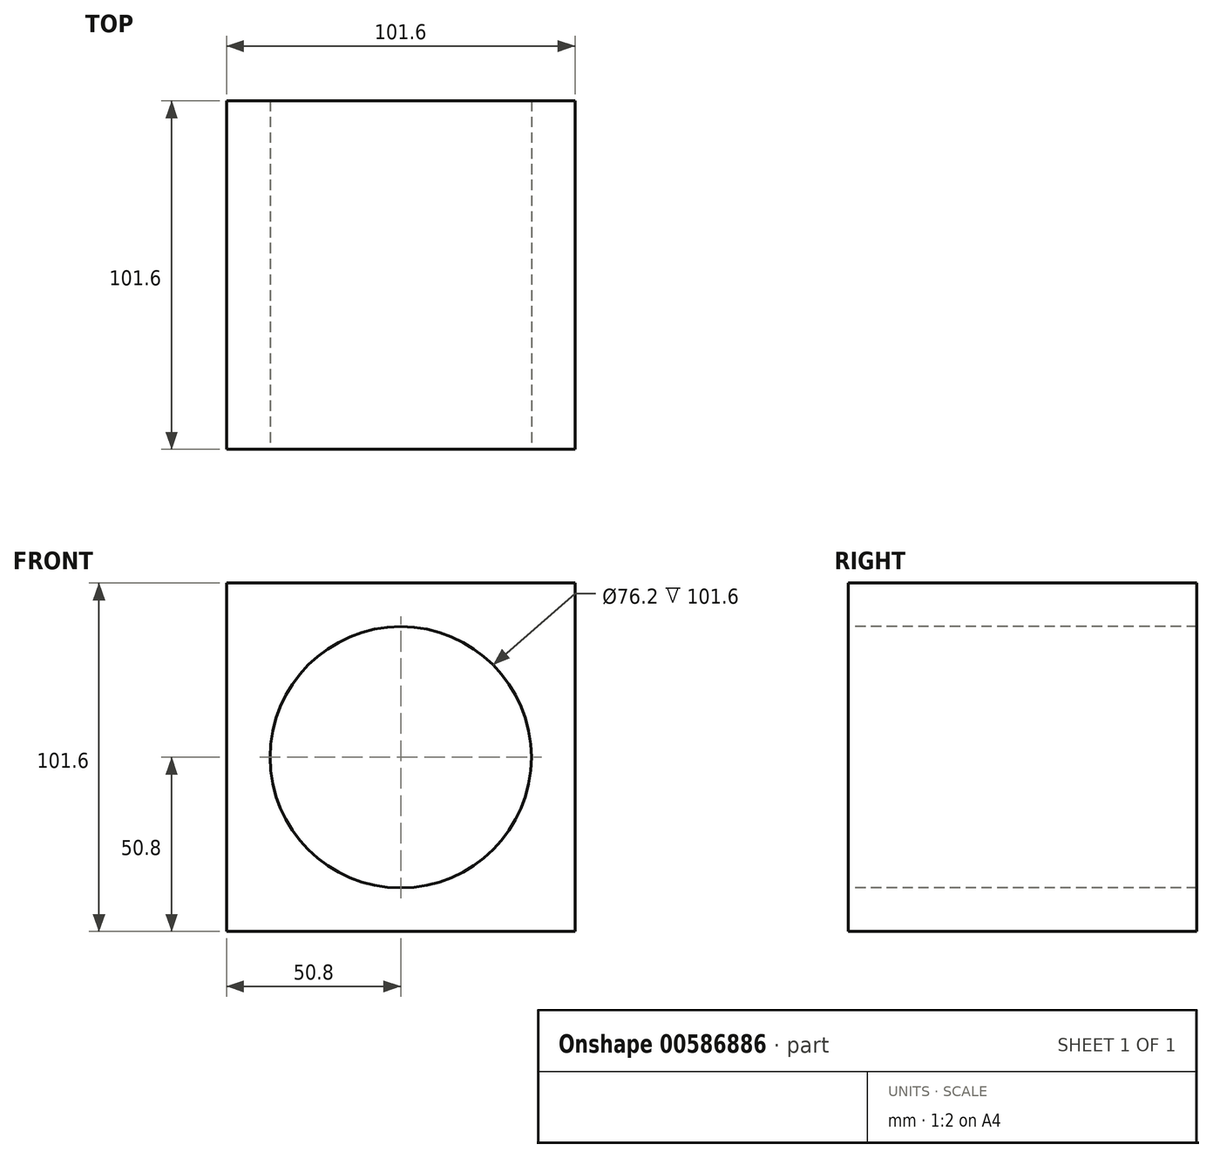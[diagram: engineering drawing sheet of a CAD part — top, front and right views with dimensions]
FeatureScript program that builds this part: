
annotation { "Feature Type Name" : "Feature", "Feature Type Description" : "" }
export const myFeature = defineFeature(function(context is Context, id is Id, definition is map)
    precondition{}
    {
        {
            var Q0;
            Q0=qCreatedBy(makeId("Front.planeOp"),FACE);
            var sketch = newSketch(context, id + "F0", { "sketchPlane" : qUnion([Q0])});
            skLineSegment(sketch, "E0.bottom", {"start": v(0, 0) * mm, "end": v(101.6, 0) * mm});
            skLineSegment(sketch, "E0.top", {"start": v(0, 101.6) * mm, "end": v(101.6, 101.6) * mm});
            skLineSegment(sketch, "E0.left", {"start": v(0, 0) * mm, "end": v(0, 101.6) * mm});
            skLineSegment(sketch, "E0.right", {"start": v(101.6, 0) * mm, "end": v(101.6, 101.6) * mm});
            skSolve(sketch);
        }
        {
            var Q0;
            Q0=makeQuery(id+"F0.imprint","IMPRINT",FACE,{"disambiguationData":[TD([[makeQuery(id+"F0.imprint","IMPRINT",EDGE,{"derivedFrom":sQuery(id+"F0.wireOp",EDGE,"E0.bottom")}),1.0]])]});
            extrude(context, id + "F1", {"entities" : qUnion([Q0]), "depth" : 101.6 * mm, "offsetDistance" : 25.4 * mm});
        }
        {
            var Q0;
            Q0=makeQuery(id+"F1.opExtrude","CAP_FACE",FACE,{"disambiguationData":[OSD([sQuery(id+"F0.wireOp",EDGE,"E0.bottom"),sQuery(id+"F0.wireOp",EDGE,"E0.top"),sQuery(id+"F0.wireOp",EDGE,"E0.left"),sQuery(id+"F0.wireOp",EDGE,"E0.right")])],"isStart":false});
            var sketch = newSketch(context, id + "F2", { "sketchPlane" : qUnion([Q0])});
            skCircle(sketch, "E1", {"center": v(50.8, 50.8) * mm, "radius": 38.1 * mm});
            skLineSegment(sketch, "E2", {"start": v(12.7, 50.8) * mm, "end": v(88.9, 50.8) * mm, "construction": true});
            skLineSegment(sketch, "E3", {"start": v(50.8, 88.9) * mm, "end": v(50.8, 50.8) * mm, "construction": true});
            skSolve(sketch);
        }
        {
            var Q0;
            Q0=makeQuery(id+"F2.imprint","IMPRINT",FACE,{"disambiguationData":[TD([[makeQuery(id+"F2.imprint","IMPRINT",EDGE,{"derivedFrom":sQuery(id+"F2.wireOp",EDGE,"E1")}),1.0]])]});
            extrude(context, id + "F3", {"entities" : qUnion([Q0]), "operationType" : NewBodyOperationType.REMOVE, "oppositeDirection" : true, "depth" : 165.1 * mm, "offsetDistance" : 25.4 * mm});
        }
    });
